# Revit family: Branch Circuit Emergency Lighting Control Transfer Switch
name_source: partatom
category: Communication Devices
revit_build: Autodesk Revit 2014 (Build: 20130308_1515(x64)
units: mm (PartAtom-declared; Revit-internal decimal feet)

## types (1)
- Branch Circuit Emergency Lighting Control Transfer Switch
    Assembly Code = D5090
    Black = Paint - Hubbell - Carbon Black
    Blue = Plastic - Hubbell - Blue
    Default Elevation = 48 "
    Description = The UL1008BCELTS1277 is specifically listed for branch circuit emergency lighting control under the new UL standards. This unit is intended for applications where both a normal and emergency branch circuit are to be connected to the emergency lighting. The UL1008BCELTS1277 automatically transfers from normal to emergency power source upon loss of normal power in the space.The UL1008BCELTS1277 allows emergency lighting to be dimmed with normal lighting during normal times. In the event of a utility power interruption, the UL1008BCELTS1277 will automatically transfer designated emergency fixtures from the dimming control to the emergency power source and bring them to full brightness, regardless of whether the dimming system is in operation or turned off.
    Features = UL1008 listed for transfer of branch circuits
Transfer includes neutral wire
Compatible with all dimming systems
Integral front mounted test swtich
Fire alarm interface option
Safety interlock system prevents cross connection
50A relay contacts allow for high inrush loads
Suitable for flush or surface mounting
    Gray = Paint - Hubbell - Gray Smooth
    Green = Paint - Hubbell - Green Textured
    Height = 4.5 "
    Manufacturer = Hubbell Control Solutions
    Model = UL1008BCELTS1277
    Product Documentation Link = https://hubbellcdn.com
    Product Page URL = https://www.hubbell.com
    Red = Paint - Hubbell - Red
    Type Comments = Branch Circuit Emergency Lighting Control Transfer Switch
    URL = https://www.hubbell.com
    Warranty = 5-Years Warranty
    Width = 2.75 "

## geometry (parser evidence)
native form markers: Sweep x1
no freeform markers — native parametric forms only
